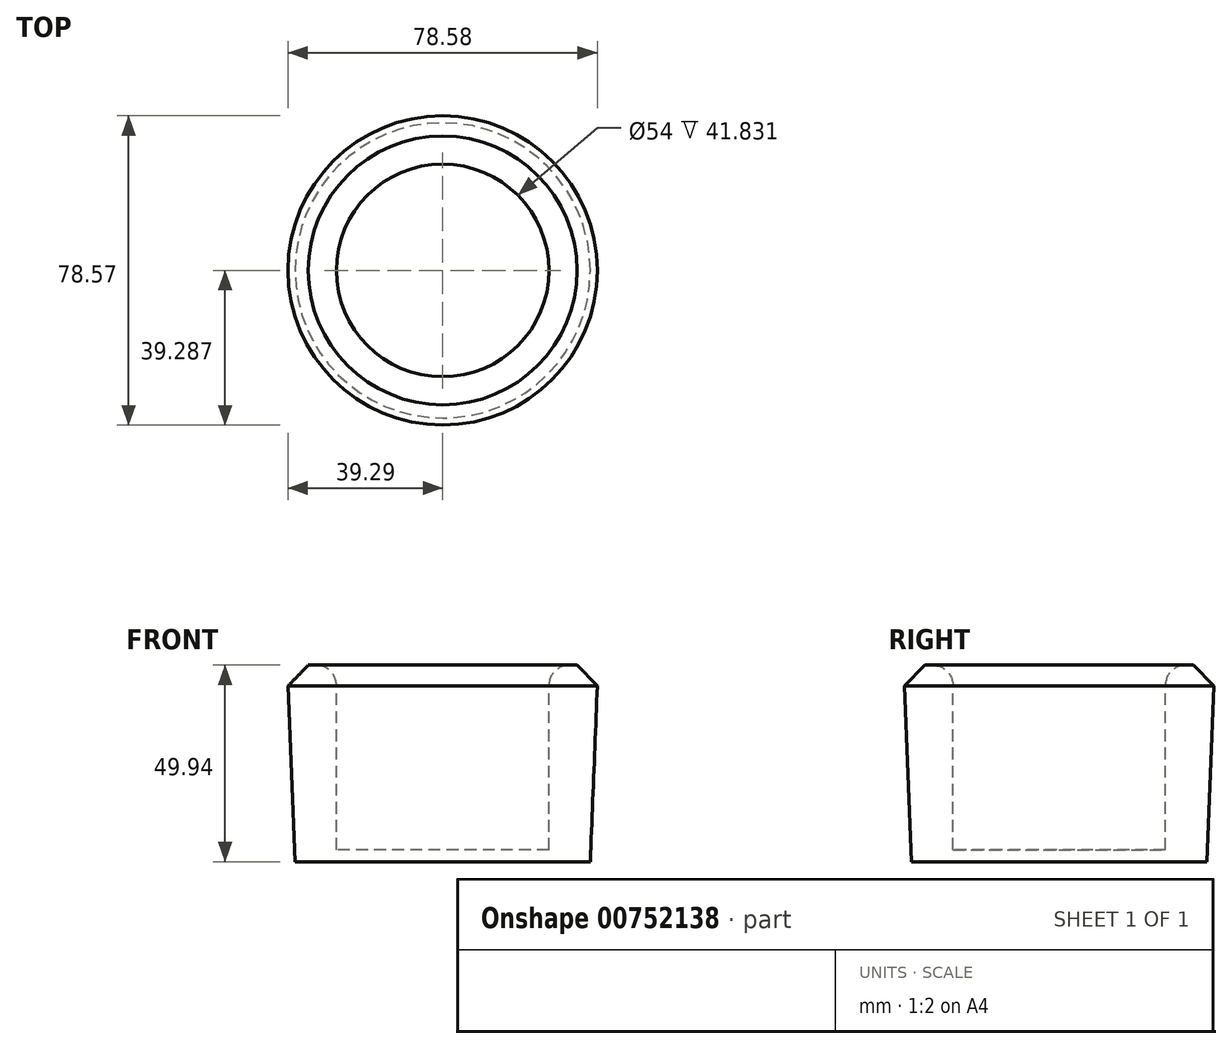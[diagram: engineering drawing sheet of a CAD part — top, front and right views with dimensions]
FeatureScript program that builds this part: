
annotation { "Feature Type Name" : "Feature", "Feature Type Description" : "" }
export const myFeature = defineFeature(function(context is Context, id is Id, definition is map)
    precondition{}
    {
        {
            var Q0;
            Q0=qCreatedBy(makeId("Right.planeOp"),FACE);
            var sketch = newSketch(context, id + "F0", { "sketchPlane" : qUnion([Q0])});
            skLineSegment(sketch, "E0", {"start": v(-52.24, 41.31) * mm, "end": v(-46.05, 41.31) * mm});
            skLineSegment(sketch, "E1", {"start": v(-46.05, 41.31) * mm, "end": v(-46.05, -5.54) * mm});
            skLineSegment(sketch, "E2", {"start": v(-46.05, -5.54) * mm, "end": v(-19.05, -5.54) * mm});
            skLineSegment(sketch, "E3", {"start": v(-19.05, -5.54) * mm, "end": v(-19.05, -8.54) * mm});
            skLineSegment(sketch, "E4", {"start": v(-19.05, -8.54) * mm, "end": v(-56.55, -8.54) * mm});
            skLineSegment(sketch, "E5", {"start": v(-56.55, -8.54) * mm, "end": v(-58.55, 41.46) * mm});
            skLineSegment(sketch, "E6", {"start": v(-58.55, 41.46) * mm, "end": v(-46.05, 41.31) * mm});
            skSolve(sketch);
        }
        {
            var Q0;
            Q0=makeQuery(id+"F0.imprint","IMPRINT",FACE,{"disambiguationData":[TD([[makeQuery(id+"F0.imprint","IMPRINT",EDGE,{"derivedFrom":sQuery(id+"F0.wireOp",EDGE,"E1")}),-1.0]])]});
            var Q1;
            Q1=sQuery(id+"F0.wireOp",EDGE,"E3");
            revolve(context, id + "F1", {"surfaceOperationType" : NewSurfaceOperationType.NEW, "entities" : qUnion([Q0]), "axis" : qUnion([Q1]), "revolveType" : RevolveType.FULL});
        }
        {
            var Q0;
            Q0=makeQuery(id+"F1.opRevolve","SWEPT_EDGE",EDGE,{"disambiguationData":[OSD([sQuery(id+"F0.wireOp",EDGE,"E1"),sQuery(id+"F0.wireOp",EDGE,"E6")])]});
            fillet(context, id + "F2", {"entities" : qUnion([Q0]), "radius" : 5.08 * mm, "tangentPropagation" : true, "allowEdgeOverflow" : false});
        }
        {
            var Q0;
            Q0=makeQuery(id+"F1.opRevolve","SWEPT_EDGE",EDGE,{"disambiguationData":[OSD([sQuery(id+"F0.wireOp",EDGE,"E5"),sQuery(id+"F0.wireOp",EDGE,"E6")])]});
            chamfer(context, id + "F3", {"entities" : qUnion([Q0]), "width" : 5.08 * mm, "tangentPropagation" : true});
        }
    });
